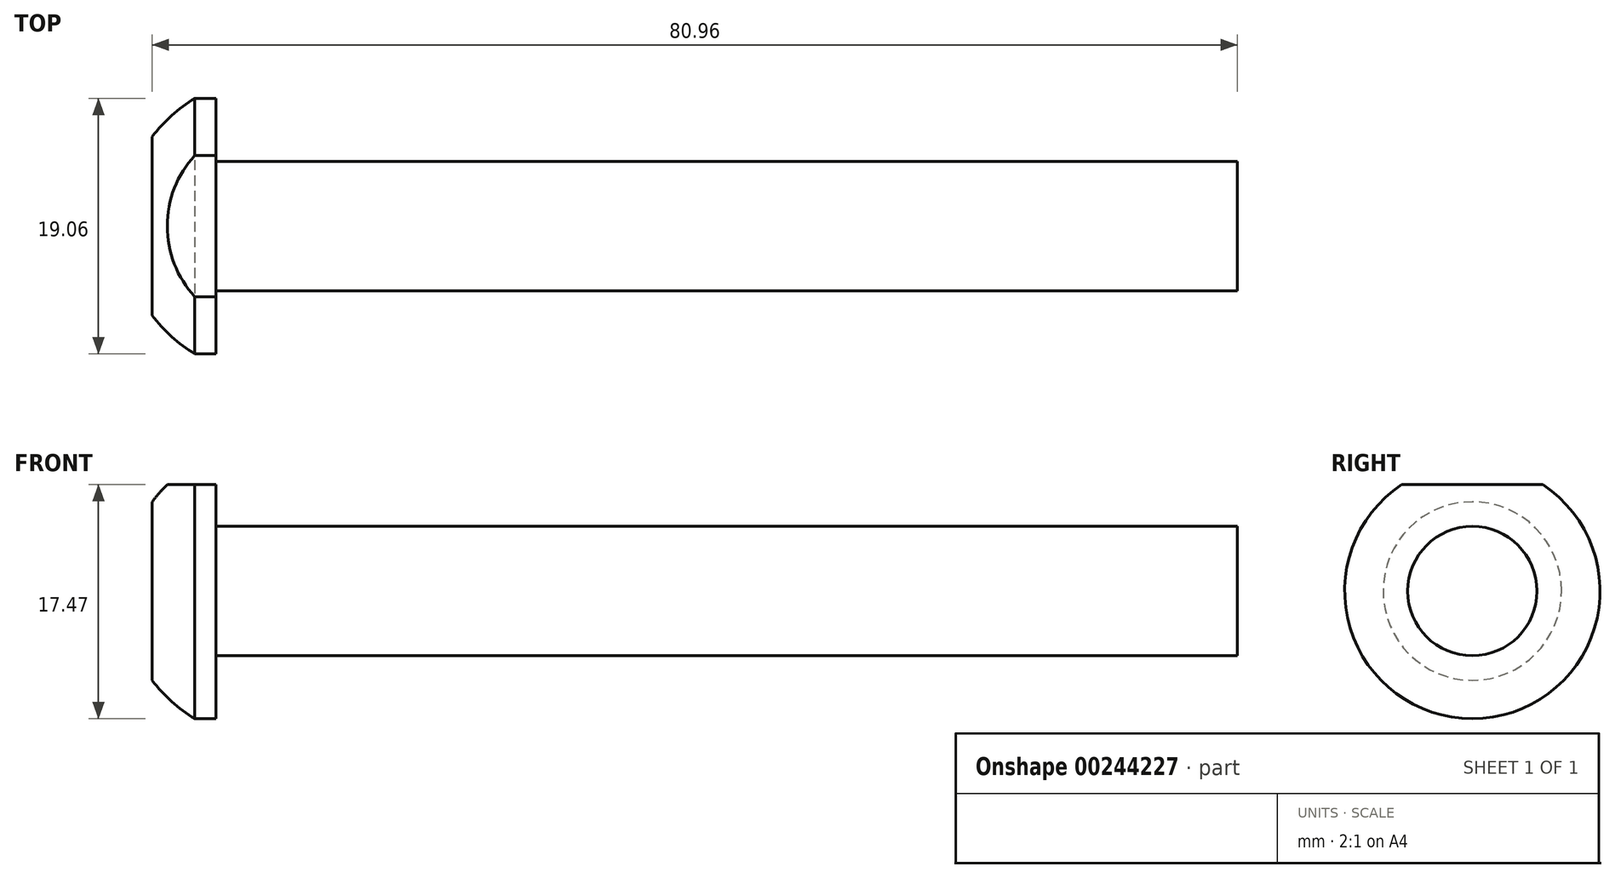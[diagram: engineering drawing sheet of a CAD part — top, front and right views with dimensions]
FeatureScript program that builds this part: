
annotation { "Feature Type Name" : "Feature", "Feature Type Description" : "" }
export const myFeature = defineFeature(function(context is Context, id is Id, definition is map)
    precondition{}
    {
        {
            var Q0;
            Q0=qCreatedBy(makeId("Front.planeOp"),FACE);
            var sketch = newSketch(context, id + "F0", { "sketchPlane" : qUnion([Q0])});
            skLineSegment(sketch, "E0.bottom", {"start": v(-422.8, 239.2) * mm, "end": v(-346.6, 239.2) * mm});
            skLineSegment(sketch, "E0.right", {"start": v(-346.6, 239.2) * mm, "end": v(-346.6, 234.38) * mm});
            skLineSegment(sketch, "E1", {"start": v(-427.57, 234.38) * mm, "end": v(-346.6, 234.38) * mm});
            skLineSegment(sketch, "E2", {"start": v(-422.8, 243.9) * mm, "end": v(-424.4, 243.9) * mm});
            skLineSegment(sketch, "E3", {"start": v(-422.8, 243.9) * mm, "end": v(-422.8, 234.38) * mm});
            skLineSegment(sketch, "E4", {"start": v(-424.4, 243.9) * mm, "end": v(-424.4, 234.38) * mm});
            skArc(sketch, "E5", {"start": v(-424.4, 243.9) * mm, "mid": v(-426.12, 242.62) * mm, "end": v(-427.57, 241.03) * mm});
            skLineSegment(sketch, "E6", {"start": v(-427.57, 234.38) * mm, "end": v(-427.57, 241.03) * mm});
            skPoint(sketch, "E7.orphan", {"position": v(-424.4, 224.85) * mm});
            skSolve(sketch);
        }
        {
            var Q0;
            Q0 = qSketchRegion(id + "F0", true);
            var Q1;
            Q1=sQuery(id+"F0.wireOp",EDGE,"E1");
            revolve(context, id + "F1", {"entities" : qUnion([Q0]), "axis" : qUnion([Q1]), "revolveType" : RevolveType.FULL});
        }
        {
            var Q0;
            Q0=makeQuery(id+"F1.opRevolve","SWEPT_FACE",FACE,{"disambiguationData":[OSD([sQuery(id+"F0.wireOp",EDGE,"E3")])]});
            var sketch = newSketch(context, id + "F2", { "sketchPlane" : qUnion([Q0])});
            skLineSegment(sketch, "E8", {"start": v(-5.27, 242.32) * mm, "end": v(5.27, 242.32) * mm});
            skPoint(sketch, "E9", {"position": v(0, 234.38) * mm});
            skLineSegment(sketch, "E10.top", {"start": v(-5.27, 247.3) * mm, "end": v(5.27, 247.3) * mm});
            skLineSegment(sketch, "E10.left", {"start": v(-5.27, 242.32) * mm, "end": v(-5.27, 247.3) * mm});
            skLineSegment(sketch, "E10.right", {"start": v(5.27, 242.32) * mm, "end": v(5.27, 247.3) * mm});
            skSolve(sketch);
        }
        {
            var Q0;
            Q0 = qSketchRegion(id + "F2", true);
            extrude(context, id + "F3", {"entities" : qUnion([Q0]), "operationType" : NewBodyOperationType.REMOVE, "oppositeDirection" : true, "depth" : 25.4 * mm});
        }
    });
